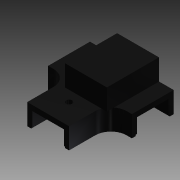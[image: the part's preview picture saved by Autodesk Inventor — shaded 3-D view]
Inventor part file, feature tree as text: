
AUTODESK INVENTOR PART (.ipt)
format: ipt  version: 2015 (Build 190159000, 159)  size: 265,216 bytes
history: native  units: in
note: dims shown in document units (in); Inventor stores cm internally (conversion verified against a paired STEP export)
features: extrude x14, sketch x14, reference x4, projected_geometry x4, other x3, plane x2, split x1, fillet x1
ambient origin geometry x8: Origin, YZ Plane, XZ Plane, XY Plane, X Axis, Y Axis, Z Axis, Center Point
bodies: Solid1 (feature_tree)
feature tree (43):
  extrude  "Extrusion1"  Depth=1.0in
  extrude  "Extrusion2"  Depth=0.5in TaperAngle=0.0deg
  extrude  "Extrusion3"  Depth=0.5in
  extrude  "Extrusion4"  Depth=1.75in TaperAngle=0.0deg
  extrude  "Extrusion5"  Depth=0.75in
  split  "Split1"
  other  "Lip1"
  other  "Lip2"
  other  "Lip3"
  extrude  "Extrusion6"  Depth=0.141in
  fillet  "Fillet1"  Radius=1.0in
  sketch  "Sketch8"  dims[d16=0.03in d17=0.03in d18=0.0in d19=0.0in d20=0.0in d21=0.0in]
  plane  "Work Plane1"
  extrude  "Extrusion7"  Depth=0.375in TaperAngle=0.0deg
  extrude  "Extrusion8"  Depth=1.0in TaperAngle=0.0deg
  extrude  "Extrusion9"  Depth=1.125in TaperAngle=0.0deg
  sketch  "Sketch12"  dims[d37=0.375in d38=0.125in d39=0.0in]
  plane  "Work Plane2"
  extrude  "Extrusion10"  Depth=3.1875in TaperAngle=0.0deg
  extrude  "Extrusion11"  [1 undecoded]
  extrude  "Extrusion12"  [1 undecoded]
  extrude  "Extrusion13"  [1 undecoded]
  extrude  "Extrusion14"  [1 undecoded]
  sketch  "Sketch1"  dims[d0=1.0in d1=1.0in]
  sketch  "Sketch2"  dims[d2=2.0in d3=0.0in d4=0.5in d5=0.0in]
  sketch  "Sketch4"  dims[d6=0.5in d7=0.0in d8=0.75in]
  sketch  "Sketch5"  dims[d9=0.75in d10=1.75in d11=0.0in]
  sketch  "Sketch6"  dims[d12=0.75in d13=0.75in]
  sketch  "Sketch7"  dims[d14=1.75in d15=0.0in]
  reference  "Reference1"
  sketch  "Sketch9"  dims[d22=0.03in d23=0.03in d24=0.0in d25=0.0in d26=0.0in d27=0.0in]
  projected_geometry  "Projected Loop1"
  sketch  "Sketch11"  dims[d28=0.03in d29=0.03in d30=0.0in d31=0.0in d32=0.0in d33=0.0in d34=0.141in d35=1.0in d36=0.0in]
  projected_geometry  "Projected Loop2"
  projected_geometry  "Projected Loop3"
  sketch  "Sketch13"  dims[d40=1.0in d41=0.0in d42=1.0in d43=0.0in]
  reference  "Reference2"
  sketch  "Sketch14"  dims[d44=1.0in d45=0.0in d46=1.125in d47=0.0in]
  reference  "Reference3"
  sketch  "Sketch15"  dims[d48=1.125in d49=0.0in d50=3.1875in d51=0.0in]
  projected_geometry  "Projected Loop5"
  reference  "Reference4"
  sketch  "Sketch16"  dims[d52=3.1875in d53=0.0in]
note: 4 required parameter values undecoded (feature->parameter linkage not recoverable at this tier; creation-order binding heuristic only, values carry confidence <= 0.55)
